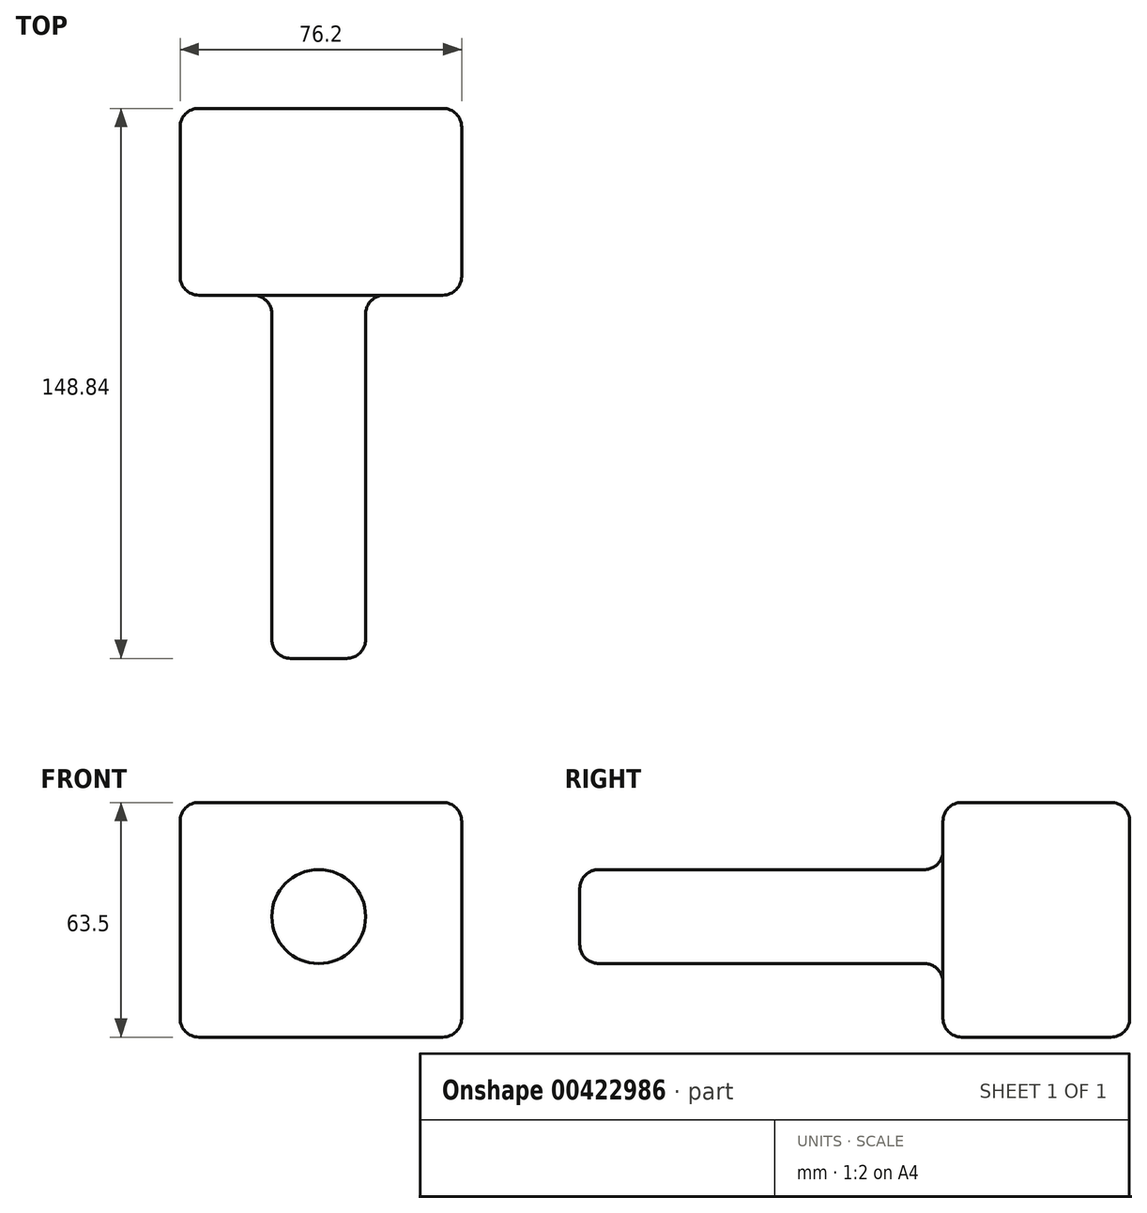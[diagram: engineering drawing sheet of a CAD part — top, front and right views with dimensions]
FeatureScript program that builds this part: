
annotation { "Feature Type Name" : "Feature", "Feature Type Description" : "" }
export const myFeature = defineFeature(function(context is Context, id is Id, definition is map)
    precondition{}
    {
        {
            var Q0;
            Q0=qCreatedBy(makeId("Front.planeOp"),FACE);
            var sketch = newSketch(context, id + "F0", { "sketchPlane" : qUnion([Q0])});
            skLineSegment(sketch, "E0.bottom", {"start": v(0, 0) * mm, "end": v(-76.2, 0) * mm});
            skLineSegment(sketch, "E0.top", {"start": v(0, 63.5) * mm, "end": v(-76.2, 63.5) * mm});
            skLineSegment(sketch, "E0.left", {"start": v(0, 0) * mm, "end": v(0, 63.5) * mm});
            skLineSegment(sketch, "E0.right", {"start": v(-76.2, 0) * mm, "end": v(-76.2, 63.5) * mm});
            skSolve(sketch);
        }
        {
            var Q0;
            Q0 = qSketchRegion(id + "F0", true);
            extrude(context, id + "F1", {"entities" : qUnion([Q0]), "depth" : 50.55 * mm});
        }
        {
            var Q0;
            Q0=makeQuery(id+"F1.opExtrude","CAP_FACE",FACE,{"disambiguationData":[OSD([sQuery(id+"F0.wireOp",EDGE,"E0.bottom"),sQuery(id+"F0.wireOp",EDGE,"E0.top"),sQuery(id+"F0.wireOp",EDGE,"E0.left"),sQuery(id+"F0.wireOp",EDGE,"E0.right")])],"isStart":false});
            var sketch = newSketch(context, id + "F2", { "sketchPlane" : qUnion([Q0])});
            skCircle(sketch, "E1", {"center": v(-38.67, 32.62) * mm, "radius": 12.7 * mm});
            skSolve(sketch);
        }
        {
            var Q0;
            Q0 = qSketchRegion(id + "F2", true);
            extrude(context, id + "F3", {"entities" : qUnion([Q0]), "operationType" : NewBodyOperationType.ADD, "depth" : 98.3 * mm});
        }
        {
            var Q0;
            Q0=makeQuery(id+"F1.opExtrude","SWEPT_EDGE",EDGE,{"disambiguationData":[OSD([sQuery(id+"F0.wireOp",EDGE,"E0.bottom"),sQuery(id+"F0.wireOp",EDGE,"E0.left")])]});
            var Q1;
            Q1=makeQuery(id+"F1.opExtrude","SWEPT_EDGE",EDGE,{"disambiguationData":[OSD([sQuery(id+"F0.wireOp",EDGE,"E0.top"),sQuery(id+"F0.wireOp",EDGE,"E0.left")])]});
            var Q2;
            Q2=makeQuery(id+"F1.opExtrude","SWEPT_EDGE",EDGE,{"disambiguationData":[OSD([sQuery(id+"F0.wireOp",EDGE,"E0.top"),sQuery(id+"F0.wireOp",EDGE,"E0.right")])]});
            var Q3;
            Q3=makeQuery(id+"F1.opExtrude","SWEPT_EDGE",EDGE,{"disambiguationData":[OSD([sQuery(id+"F0.wireOp",EDGE,"E0.bottom"),sQuery(id+"F0.wireOp",EDGE,"E0.right")])]});
            fillet(context, id + "F4", {"entities" : qUnion([Q0, Q1, Q2, Q3]), "radius" : 5.08 * mm, "tangentPropagation" : true, "allowEdgeOverflow" : false});
        }
        {
            var Q0;
            Q0=makeQuery(id+"F1.opExtrude","CAP_EDGE",EDGE,{"disambiguationData":[OSD([sQuery(id+"F0.wireOp",EDGE,"E0.bottom")])],"isStart":false});
            var Q1;
            Q1=makeQuery(id+"F1.opExtrude","CAP_EDGE",EDGE,{"disambiguationData":[OSD([sQuery(id+"F0.wireOp",EDGE,"E0.bottom")])],"isStart":true});
            fillet(context, id + "F5", {"entities" : qUnion([Q0, Q1]), "radius" : 5.08 * mm, "tangentPropagation" : true, "allowEdgeOverflow" : false});
        }
        {
            var Q0;
            Q0=makeQuery(id+"F3.opExtrude","SWEPT_FACE",FACE,{"disambiguationData":[OSD([sQuery(id+"F2.wireOp",EDGE,"E1")])]});
            fillet(context, id + "F6", {"entities" : qUnion([Q0]), "radius" : 5.08 * mm, "tangentPropagation" : true, "allowEdgeOverflow" : false});
        }
    });
